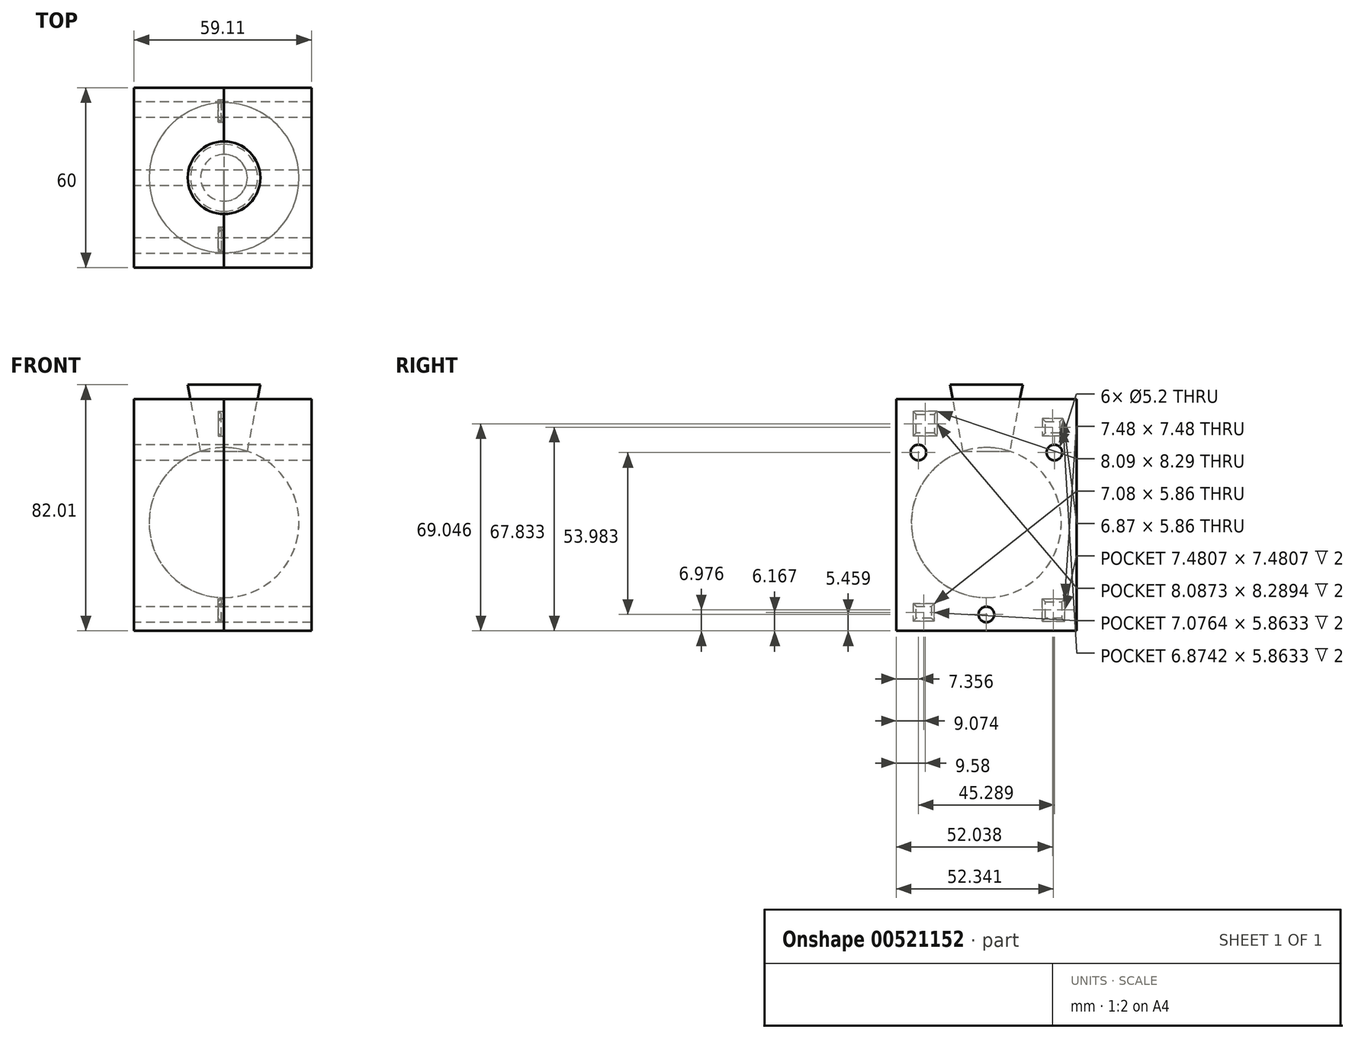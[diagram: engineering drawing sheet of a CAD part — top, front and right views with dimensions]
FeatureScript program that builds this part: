
annotation { "Feature Type Name" : "Feature", "Feature Type Description" : "" }
export const myFeature = defineFeature(function(context is Context, id is Id, definition is map)
    precondition{}
    {
        {
            var Q0;
            Q0=qCreatedBy(makeId("Front.planeOp"),FACE);
            var sketch = newSketch(context, id + "F0", { "sketchPlane" : qUnion([Q0])});
            skArc(sketch, "E0", {"start": v(0, 25) * mm, "mid": v(-25, 0) * mm, "end": v(0, -25) * mm});
            skLineSegment(sketch, "E1", {"start": v(0, -32.14) * mm, "end": v(0, 35.51) * mm});
            skSolve(sketch);
        }
        {
            var Q0;
            {var subQ0=sQuery(id+"F0.wireOp",EDGE,"E0");Q0=makeQuery(id+"F0.imprint","IMPRINT",FACE,{"disambiguationData":[TD([[makeQuery(id+"F0.imprint","IMPRINT",EDGE,{"derivedFrom":subQ0}),1.0]])]});}
            var Q1;
            Q1=sQuery(id+"F0.wireOp",EDGE,"E1");
            revolve(context, id + "F1", {"entities" : qUnion([Q0]), "axis" : qUnion([Q1]), "revolveType" : RevolveType.FULL});
        }
        {
            var Q0;
            Q0=qCreatedBy(makeId("Front.planeOp"),FACE);
            var sketch = newSketch(context, id + "F2", { "sketchPlane" : qUnion([Q0])});
            skLineSegment(sketch, "E2.bottom", {"start": v(0, 41.14) * mm, "end": v(29.11, 41.14) * mm});
            skLineSegment(sketch, "E2.top", {"start": v(0, -36.09) * mm, "end": v(29.11, -36.09) * mm});
            skLineSegment(sketch, "E2.left", {"start": v(0, 41.14) * mm, "end": v(0, -36.09) * mm});
            skLineSegment(sketch, "E2.right", {"start": v(29.11, 41.14) * mm, "end": v(29.11, -36.09) * mm});
            skSolve(sketch);
        }
        {
            var Q0;
            Q0=makeQuery(id+"F2.imprint","IMPRINT",FACE,{"disambiguationData":[TD([[makeQuery(id+"F2.imprint","IMPRINT",EDGE,{"derivedFrom":sQuery(id+"F2.wireOp",EDGE,"E2.bottom")}),-1.0]])]});
            extrude(context, id + "F3", {"entities" : qUnion([Q0]), "endBound" : BoundingType.SYMMETRIC, "oppositeDirection" : true, "depth" : 60 * mm, "offsetDistance" : 25 * mm});
        }
        {
            var Q0;
            Q0=makeQuery(id+"F3.opExtrude","SWEPT_FACE",FACE,{"disambiguationData":[OSD([sQuery(id+"F2.wireOp",EDGE,"E2.left")])]});
            var sketch = newSketch(context, id + "F4", { "sketchPlane" : qUnion([Q0])});
            skLineSegment(sketch, "E3.bottom", {"start": v(-25.47, 34.67) * mm, "end": v(-18.6, 34.67) * mm});
            skLineSegment(sketch, "E3.top", {"start": v(-25.47, 28.81) * mm, "end": v(-18.6, 28.81) * mm});
            skLineSegment(sketch, "E3.left", {"start": v(-25.47, 34.67) * mm, "end": v(-25.47, 28.81) * mm});
            skLineSegment(sketch, "E3.right", {"start": v(-18.6, 34.67) * mm, "end": v(-18.6, 28.81) * mm});
            skLineSegment(sketch, "E4.bottom", {"start": v(17.39, -27) * mm, "end": v(24.46, -27) * mm});
            skLineSegment(sketch, "E4.top", {"start": v(17.39, -32.85) * mm, "end": v(24.46, -32.85) * mm});
            skLineSegment(sketch, "E4.left", {"start": v(17.39, -27) * mm, "end": v(17.39, -32.85) * mm});
            skLineSegment(sketch, "E4.right", {"start": v(24.46, -27) * mm, "end": v(24.46, -32.85) * mm});
            skLineSegment(sketch, "E5.bottom", {"start": v(16.38, 37.1) * mm, "end": v(24.46, 37.1) * mm});
            skLineSegment(sketch, "E5.top", {"start": v(16.38, 28.81) * mm, "end": v(24.46, 28.81) * mm});
            skLineSegment(sketch, "E5.left", {"start": v(16.38, 37.1) * mm, "end": v(16.38, 28.81) * mm});
            skLineSegment(sketch, "E5.right", {"start": v(24.46, 37.1) * mm, "end": v(24.46, 28.81) * mm});
            skLineSegment(sketch, "E6.bottom", {"start": v(-18.6, -32.85) * mm, "end": v(-26.08, -32.85) * mm});
            skLineSegment(sketch, "E6.top", {"start": v(-18.6, -25.37) * mm, "end": v(-26.08, -25.37) * mm});
            skLineSegment(sketch, "E6.left", {"start": v(-18.6, -32.85) * mm, "end": v(-18.6, -25.37) * mm});
            skLineSegment(sketch, "E6.right", {"start": v(-26.08, -32.85) * mm, "end": v(-26.08, -25.37) * mm});
            skSolve(sketch);
        }
        {
            var Q0;
            Q0=makeQuery(id+"F4.imprint","IMPRINT",FACE,{"disambiguationData":[TD([[makeQuery(id+"F4.imprint","IMPRINT",EDGE,{"derivedFrom":sQuery(id+"F4.wireOp",EDGE,"E3.bottom")}),-1.0]])]});
            var Q1;
            Q1=makeQuery(id+"F4.imprint","IMPRINT",FACE,{"disambiguationData":[TD([[makeQuery(id+"F4.imprint","IMPRINT",EDGE,{"derivedFrom":sQuery(id+"F4.wireOp",EDGE,"E5.bottom")}),-1.0]])]});
            var Q2;
            Q2=makeQuery(id+"F4.imprint","IMPRINT",FACE,{"disambiguationData":[TD([[makeQuery(id+"F4.imprint","IMPRINT",EDGE,{"derivedFrom":sQuery(id+"F4.wireOp",EDGE,"E4.bottom")}),-1.0]])]});
            var Q3;
            Q3=makeQuery(id+"F4.imprint","IMPRINT",FACE,{"disambiguationData":[TD([[makeQuery(id+"F4.imprint","IMPRINT",EDGE,{"derivedFrom":sQuery(id+"F4.wireOp",EDGE,"E6.bottom")}),-1.0]])]});
            extrude(context, id + "F5", {"entities" : qUnion([Q0, Q1, Q2, Q3]), "operationType" : NewBodyOperationType.ADD, "depth" : 2 * mm, "offsetDistance" : 25 * mm});
        }
        {
            var Q0;
            Q0=makeQuery(id+"F3.opExtrude","SWEPT_FACE",FACE,{"disambiguationData":[OSD([sQuery(id+"F2.wireOp",EDGE,"E2.left")])]});
            var sketch = newSketch(context, id + "F6", { "sketchPlane" : qUnion([Q0])});
            skLineSegment(sketch, "E7.bottom", {"start": v(-30, 41.14) * mm, "end": v(30, 41.14) * mm});
            skLineSegment(sketch, "E7.top", {"start": v(-30, -36.09) * mm, "end": v(30, -36.09) * mm});
            skLineSegment(sketch, "E7.left", {"start": v(-30, 41.14) * mm, "end": v(-30, -36.09) * mm});
            skLineSegment(sketch, "E7.right", {"start": v(30, 41.14) * mm, "end": v(30, -36.09) * mm});
            skSolve(sketch);
        }
        {
            var Q0;
            Q0=makeQuery(id+"F1.opRevolve","SWEPT_BODY",BODY,{"disambiguationData":[OSD([sQuery(id+"F0.wireOp",EDGE,"E0"),sQuery(id+"F0.wireOp",EDGE,"E1")])]});
            var Q1;
            Q1=makeQuery(id+"F3.opExtrude","SWEPT_BODY",BODY,{"disambiguationData":[OSD([sQuery(id+"F2.wireOp",EDGE,"E2.bottom"),sQuery(id+"F2.wireOp",EDGE,"E2.top"),sQuery(id+"F2.wireOp",EDGE,"E2.left"),sQuery(id+"F2.wireOp",EDGE,"E2.right")])]});
            booleanBodies(context, id + "F7", {"operationType" : BooleanOperationType.SUBTRACTION, "tools" : qUnion([Q0]), "targets" : qUnion([Q1]), "keepTools" : true});
        }
        {
            var Q0;
            Q0 = qSketchRegion(id + "F6", true);
            extrude(context, id + "F8", {"entities" : qUnion([Q0]), "depth" : 30 * mm, "offsetDistance" : 25 * mm});
        }
        {
            var Q0;
            Q0=makeQuery(id+"F3.opExtrude","SWEPT_BODY",BODY,{"disambiguationData":[OSD([sQuery(id+"F2.wireOp",EDGE,"E2.bottom"),sQuery(id+"F2.wireOp",EDGE,"E2.top"),sQuery(id+"F2.wireOp",EDGE,"E2.left"),sQuery(id+"F2.wireOp",EDGE,"E2.right")])]});
            var Q1;
            Q1=makeQuery(id+"F8.opExtrude","SWEPT_BODY",BODY,{"disambiguationData":[OSD([sQuery(id+"F6.wireOp",EDGE,"E7.bottom"),sQuery(id+"F6.wireOp",EDGE,"E7.top"),sQuery(id+"F6.wireOp",EDGE,"E7.left"),sQuery(id+"F6.wireOp",EDGE,"E7.right")])]});
            booleanBodies(context, id + "F9", {"operationType" : BooleanOperationType.SUBTRACTION, "tools" : qUnion([Q0]), "targets" : qUnion([Q1]), "keepTools" : true});
        }
        {
            var Q0;
            Q0=makeQuery(id+"F1.opRevolve","SWEPT_BODY",BODY,{"disambiguationData":[OSD([sQuery(id+"F0.wireOp",EDGE,"E0"),sQuery(id+"F0.wireOp",EDGE,"E1")])]});
            var Q1;
            Q1=makeQuery(id+"F8.opExtrude","SWEPT_BODY",BODY,{"disambiguationData":[OSD([sQuery(id+"F6.wireOp",EDGE,"E7.bottom"),sQuery(id+"F6.wireOp",EDGE,"E7.top"),sQuery(id+"F6.wireOp",EDGE,"E7.left"),sQuery(id+"F6.wireOp",EDGE,"E7.right")])]});
            booleanBodies(context, id + "F10", {"operationType" : BooleanOperationType.SUBTRACTION, "tools" : qUnion([Q0]), "targets" : qUnion([Q1]), "keepTools" : true});
        }
        {
            var Q0;
            Q0=makeQuery(id+"F3.opExtrude","SWEPT_FACE",FACE,{"disambiguationData":[OSD([sQuery(id+"F2.wireOp",EDGE,"E2.left")])]});
            var sketch = newSketch(context, id + "F11", { "sketchPlane" : qUnion([Q0])});
            skLineSegment(sketch, "E8", {"start": v(-6.87, 19.1) * mm, "end": v(0, 19.1) * mm});
            skLineSegment(sketch, "E9", {"start": v(-6.87, 19.1) * mm, "end": v(-12.1, 45.92) * mm});
            skLineSegment(sketch, "E10", {"start": v(-12.1, 45.92) * mm, "end": v(0, 45.92) * mm});
            skLineSegment(sketch, "E11", {"start": v(0, 45.92) * mm, "end": v(0, 19.1) * mm});
            skSolve(sketch);
        }
        {
            var Q0;
            {var subQ0=sQuery(id+"F11.wireOp",EDGE,"E10");Q0=makeQuery(id+"F11.imprint","IMPRINT",FACE,{"disambiguationData":[TD([[makeQuery(id+"F11.imprint","IMPRINT",EDGE,{"derivedFrom":subQ0}),-1.0]])]});}
            var Q1;
            {var subQ0=sQuery(id+"F11.wireOp",EDGE,"E9");var subQ1=sQuery(id+"F2.wireOp",EDGE,"E2.left");var subQ2=makeQuery(id+"F3.opExtrude","SWEPT_EDGE",EDGE,{"disambiguationData":[OSD([sQuery(id+"F2.wireOp",EDGE,"E2.bottom"),subQ1])]});var subQ3=makeQuery(id+"F11.imprint","INTERSECT",VERTEX,{"derivedFrom":[subQ2,subQ0]});Q1=makeQuery(id+"F11.imprint","IMPRINT",FACE,{"disambiguationData":[TD([[makeQuery(id+"F11.imprint","IMPRINT",EDGE,{"disambiguationData":[TD([[subQ3,1.0]])],"derivedFrom":subQ0}),-1.0]])]});}
            var Q2;
            Q2=sQuery(id+"F11.wireOp",EDGE,"E11");
            revolve(context, id + "F12", {"entities" : qUnion([Q0, Q1]), "axis" : qUnion([Q2]), "revolveType" : RevolveType.FULL});
        }
        {
            var Q0;
            Q0=makeQuery(id+"F1.opRevolve","SWEPT_BODY",BODY,{"disambiguationData":[OSD([sQuery(id+"F0.wireOp",EDGE,"E0"),sQuery(id+"F0.wireOp",EDGE,"E1")])]});
            var Q1;
            Q1=makeQuery(id+"F12.opRevolve","SWEPT_BODY",BODY,{"disambiguationData":[OSD([sQuery(id+"F0.wireOp",EDGE,"E0"),sQuery(id+"F2.wireOp",EDGE,"E2.left"),sQuery(id+"F11.wireOp",EDGE,"E9"),sQuery(id+"F11.wireOp",EDGE,"E10"),sQuery(id+"F11.wireOp",EDGE,"E11")])]});
            booleanBodies(context, id + "F13", {"operationType" : BooleanOperationType.SUBTRACTION, "tools" : qUnion([Q0]), "targets" : qUnion([Q1]), "keepTools" : true});
        }
        {
            var Q0;
            Q0=makeQuery(id+"F12.opRevolve","SWEPT_BODY",BODY,{"disambiguationData":[OSD([sQuery(id+"F0.wireOp",EDGE,"E0"),sQuery(id+"F2.wireOp",EDGE,"E2.left"),sQuery(id+"F11.wireOp",EDGE,"E9"),sQuery(id+"F11.wireOp",EDGE,"E10"),sQuery(id+"F11.wireOp",EDGE,"E11")])]});
            var Q1;
            Q1=makeQuery(id+"F3.opExtrude","SWEPT_BODY",BODY,{"disambiguationData":[OSD([sQuery(id+"F2.wireOp",EDGE,"E2.bottom"),sQuery(id+"F2.wireOp",EDGE,"E2.top"),sQuery(id+"F2.wireOp",EDGE,"E2.left"),sQuery(id+"F2.wireOp",EDGE,"E2.right")])]});
            var Q2;
            Q2=makeQuery(id+"F8.opExtrude","SWEPT_BODY",BODY,{"disambiguationData":[OSD([sQuery(id+"F6.wireOp",EDGE,"E7.bottom"),sQuery(id+"F6.wireOp",EDGE,"E7.top"),sQuery(id+"F6.wireOp",EDGE,"E7.left"),sQuery(id+"F6.wireOp",EDGE,"E7.right")])]});
            booleanBodies(context, id + "F14", {"operationType" : BooleanOperationType.SUBTRACTION, "tools" : qUnion([Q0]), "targets" : qUnion([Q1, Q2]), "keepTools" : true});
        }
        {
            var Q0;
            Q0=makeQuery(id+"F5.opExtrude","CAP_FACE",FACE,{"disambiguationData":[OSD([sQuery(id+"F4.wireOp",EDGE,"E5.bottom"),sQuery(id+"F4.wireOp",EDGE,"E5.top"),sQuery(id+"F4.wireOp",EDGE,"E5.left"),sQuery(id+"F4.wireOp",EDGE,"E5.right")])],"isStart":false});
            var Q1;
            Q1=makeQuery(id+"F5.opExtrude","CAP_FACE",FACE,{"disambiguationData":[OSD([sQuery(id+"F4.wireOp",EDGE,"E3.bottom"),sQuery(id+"F4.wireOp",EDGE,"E3.top"),sQuery(id+"F4.wireOp",EDGE,"E3.left"),sQuery(id+"F4.wireOp",EDGE,"E3.right")])],"isStart":false});
            var Q2;
            Q2=makeQuery(id+"F5.opExtrude","CAP_FACE",FACE,{"disambiguationData":[OSD([sQuery(id+"F4.wireOp",EDGE,"E6.bottom"),sQuery(id+"F4.wireOp",EDGE,"E6.top"),sQuery(id+"F4.wireOp",EDGE,"E6.left"),sQuery(id+"F4.wireOp",EDGE,"E6.right")])],"isStart":false});
            var Q3;
            Q3=makeQuery(id+"F5.opExtrude","CAP_FACE",FACE,{"disambiguationData":[OSD([sQuery(id+"F4.wireOp",EDGE,"E4.bottom"),sQuery(id+"F4.wireOp",EDGE,"E4.top"),sQuery(id+"F4.wireOp",EDGE,"E4.left"),sQuery(id+"F4.wireOp",EDGE,"E4.right")])],"isStart":false});
            chamfer(context, id + "F15", {"entities" : qUnion([Q0, Q1, Q2, Q3]), "width" : 1 * mm, "tangentPropagation" : true});
        }
        {
            var Q0;
            Q0=makeQuery(id+"F8.opExtrude","CAP_FACE",FACE,{"disambiguationData":[OSD([sQuery(id+"F6.wireOp",EDGE,"E7.bottom"),sQuery(id+"F6.wireOp",EDGE,"E7.top"),sQuery(id+"F6.wireOp",EDGE,"E7.left"),sQuery(id+"F6.wireOp",EDGE,"E7.right")])],"isStart":false});
            var sketch = newSketch(context, id + "F16", { "sketchPlane" : qUnion([Q0])});
            skPoint(sketch, "E12", {"position": v(0, -30.63) * mm});
            skPoint(sketch, "E13", {"position": v(22.64, 23.35) * mm});
            skLineSegment(sketch, "E14", {"start": v(0, 41.14) * mm, "end": v(0, -36.09) * mm});
            skPoint(sketch, "E15.MirrorP", {"position": v(-22.64, 23.35) * mm});
            skSolve(sketch);
        }
        {
            var Q0;
            Q0=sQuery(id+"F16.wireOp",VERTEX,"E15.MirrorP");
            var Q1;
            Q1=sQuery(id+"F16.wireOp",VERTEX,"E13");
            var Q2;
            Q2=sQuery(id+"F16.wireOp",VERTEX,"E12");
            var Q3;
            Q3=makeQuery(id+"F3.opExtrude","SWEPT_BODY",BODY,{"disambiguationData":[OSD([sQuery(id+"F2.wireOp",EDGE,"E2.bottom"),sQuery(id+"F2.wireOp",EDGE,"E2.top"),sQuery(id+"F2.wireOp",EDGE,"E2.left"),sQuery(id+"F2.wireOp",EDGE,"E2.right")])]});
            var Q4;
            Q4=makeQuery(id+"F8.opExtrude","SWEPT_BODY",BODY,{"disambiguationData":[OSD([sQuery(id+"F6.wireOp",EDGE,"E7.bottom"),sQuery(id+"F6.wireOp",EDGE,"E7.top"),sQuery(id+"F6.wireOp",EDGE,"E7.left"),sQuery(id+"F6.wireOp",EDGE,"E7.right")])]});
            hole(context, id + "F17", {"style" : HoleStyle.SIMPLE, "endStyle" : HoleEndStyle.THROUGH, "holeDiameter" : 5.2 * mm, "isTappedThrough" : true, "tappedDepth" : 12 * mm, "tapClearance" : 3, "locations" : qUnion([Q0, Q1, Q2]), "scope" : qUnion([Q3, Q4])});
        }
    });
